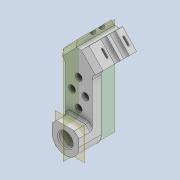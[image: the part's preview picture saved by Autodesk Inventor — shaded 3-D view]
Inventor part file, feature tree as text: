
AUTODESK INVENTOR PART (.ipt)
format: ipt  version: 2020 (Build 240168000, 168)  size: 407,552 bytes
history: native  units: mm
features: extrude x11, sketch x11, projected_geometry x8, thicken_offset x7, chamfer x4, fillet x4, other x4, plane x2, mirror x2, reference x2
ambient origin geometry x8: Origin, YZ Plane, XZ Plane, XY Plane, X Axis, Y Axis, Z Axis, Center Point
bodies: Solid1 (feature_tree)
feature tree (55):
  extrude  "Extrusion1"  Depth=30.0mm
  extrude  "Extrusion2"  Depth=10.0mm TaperAngle=0.0deg
  chamfer  "Chamfer1"  Distance=6.0mm
  extrude  "Extrusion3"  Depth=3.0mm TaperAngle=0.0deg
  extrude  "Extrusion4"  Depth=10.0mm
  extrude  "Extrusion5"  Depth=10.0mm
  thicken_offset  "Thicken1"
  thicken_offset  "Thicken2"
  extrude  "Extrusion6"  Depth=15.0mm TaperAngle=0.0deg
  extrude  "Extrusion7"  Depth=1.0mm
  chamfer  "Chamfer2"  Distance=2.5mm
  extrude  "Extrusion8"  Depth=15.0mm TaperAngle=0.0deg
  plane  "Work Plane2"
  mirror  "Mirror2"
  thicken_offset  "Thicken3"
  thicken_offset  "Thicken4"
  fillet  "Fillet2"  Radius=2.5mm
  fillet  "Fillet3"  Radius=15.0mm
  extrude  "Extrusion9"  Depth=1.0mm TaperAngle=45.0deg
  mirror  "Mirror3"
  fillet  "Fillet4"  Radius=15.0mm
  plane  "Work Plane3"
  extrude  "Extrusion10"  Depth=1.0mm
  chamfer  "Chamfer3"  Distance=1.0mm
  thicken_offset  "Thicken5"
  extrude  "Extrusion11"  Depth=1.0mm
  fillet  "Fillet5"  Radius=2.0mm
  chamfer  "Chamfer4"  Distance=3.0mm
  thicken_offset  "Thicken6"
  thicken_offset  "Thicken7"
  sketch  "Sketch1"  dims[d0=6.0mm d1=30.0mm]
  sketch  "Sketch2"  dims[d2=12.0mm d3=10.0mm d4=0.0mm]
  projected_geometry  "Projected Loop1"
  sketch  "Sketch3"  dims[d5=13.0mm]
  projected_geometry  "Projected Loop2"
  sketch  "Sketch4"  dims[d6=27.0mm d7=6.0mm d8=0.0mm]
  projected_geometry  "Projected Loop3"
  reference  "Reference1"
  sketch  "Sketch5"  dims[d9=3.0mm d10=2.0mm d11=45.0deg d12=6.0mm d13=0.0mm]
  projected_geometry  "Projected Loop4"
  sketch  "Sketch6"  dims[d14=10.0mm d15=4.0mm]
  sketch  "Sketch7"  dims[d16=10.0mm d17=4.0mm]
  sketch  "Sketch8"  dims[d18=15.0mm d19=0.0mm d20=15.0mm d21=0.0mm]
  reference  "Reference2"
  projected_geometry  "Projected Loop5"
  sketch  "Sketch9"  dims[d22=1.0mm d23=1.0mm]
  projected_geometry  "Projected Loop6"
  projected_geometry  "Projected Loop7"
  sketch  "Sketch10"  dims[d24=1.0mm]
  sketch  "Sketch11"  dims[d25=1.0mm d27=2.5mm d28=15.0mm d29=0.0mm d30=2.5mm d31=15.0mm d32=0.0mm d33=2.0mm d34=2.0mm d35=45.0deg d36=15.0mm d37=0.0mm d38=1.0mm d39=1.0mm d40=2.0mm d41=2.0mm d42=3.0mm d43=3.0mm d44=1.5mm d45=0.7mm d46=9.5mm d47=1.5mm d48=0.7mm d49=15.0mm d50=0.0mm d51=2.0mm d52=-2.0mm d53=1.0mm d54=6.0mm d55=0.0mm d56=1.0mm d57=2.0mm d58=45.0deg d59=1.0mm d60=1.0mm d61=5.0mm d62=6.0mm d63=12.0mm d64=3.0mm d65=3.0mm d66=3.0mm d67=3.0mm d68=3.0mm d69=3.0mm d70=3.0mm d71=6.0mm d72=0.0mm d73=1.0mm d74=0.5mm d75=2.0mm d76=45.0deg d77=0.05mm d78=0.05mm d79=0.05mm d80=0.05mm]
  projected_geometry  "Projected Loop8"
  parser-record x1  (decoder bookkeeping rows leaked as tree rows — omitted from the tree; the rows remain in map.json)
  other  "driver_ass_1.iam"
  other  "driver_wheel_1:1"
  other  "driver_wheel_1:2"
note: 1 file-system path scrubbed to <path> (originals preserved in map.json)
